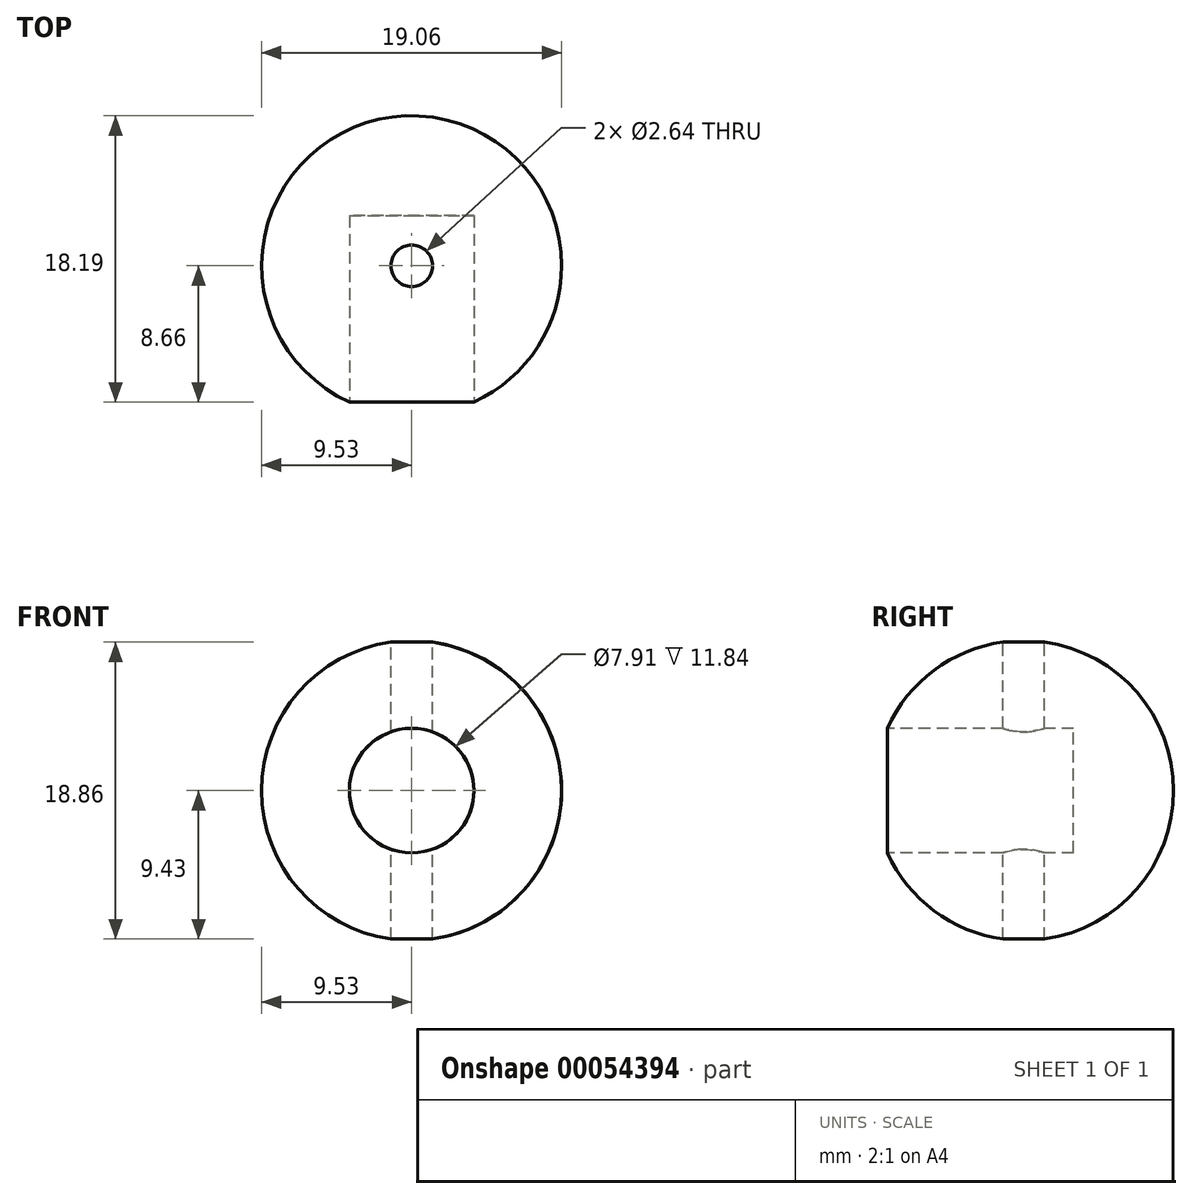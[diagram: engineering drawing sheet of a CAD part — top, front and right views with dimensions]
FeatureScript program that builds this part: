
annotation { "Feature Type Name" : "Feature", "Feature Type Description" : "" }
export const myFeature = defineFeature(function(context is Context, id is Id, definition is map)
    precondition{}
    {
        {
            var Q0;
            Q0=qCreatedBy(makeId("Front.planeOp"),FACE);
            var sketch = newSketch(context, id + "F0", { "sketchPlane" : qUnion([Q0])});
            skArc(sketch, "E0", {"start": v(0, -9.53) * mm, "mid": v(9.53, 0) * mm, "end": v(0, 9.53) * mm});
            skLineSegment(sketch, "E1", {"start": v(0, 9.53) * mm, "end": v(0, -9.53) * mm});
            skLineSegment(sketch, "E2", {"start": v(0, 0) * mm, "end": v(28.29, 0) * mm, "construction": true});
            skPoint(sketch, "E2.endSnap0", {"position": v(9.53, 0) * mm});
            skLineSegment(sketch, "E3", {"start": v(28.29, 0) * mm, "end": v(0, 0) * mm, "construction": true});
            skLineSegment(sketch, "E4", {"start": v(0, 0) * mm, "end": v(-27.51, 0) * mm, "construction": true});
            skSolve(sketch);
        }
        {
            var Q0;
            Q0=makeQuery(id+"F0.imprint","IMPRINT",FACE,{"disambiguationData":[TD([[makeQuery(id+"F0.imprint","IMPRINT",EDGE,{"derivedFrom":sQuery(id+"F0.wireOp",EDGE,"E0")}),1.0]])]});
            var Q1;
            Q1=sQuery(id+"F0.wireOp",EDGE,"E1");
            revolve(context, id + "F1", {"entities" : qUnion([Q0]), "axis" : qUnion([Q1]), "revolveType" : RevolveType.FULL});
        }
        {
            var Q0;
            Q0=qCreatedBy(makeId("Front.planeOp"),FACE);
            cPlane(context, id + "F2", {"entities" : qUnion([Q0]), "cplaneType" : CPlaneType.OFFSET, "offset" : 9.52 * mm, "width" : 152.4 * mm, "height" : 152.4 * mm});
        }
        {
            var Q0;
            Q0=qCreatedBy(id+"F2.planeOp",FACE);
            var sketch = newSketch(context, id + "F3", { "sketchPlane" : qUnion([Q0])});
            skCircle(sketch, "E5", {"center": v(0, 0) * mm, "radius": 3.96 * mm});
            skSolve(sketch);
        }
        {
            var Q0;
            Q0 = qSketchRegion(id + "F3", true);
            extrude(context, id + "F4", {"entities" : qUnion([Q0]), "operationType" : NewBodyOperationType.REMOVE, "oppositeDirection" : true, "depth" : 12.7 * mm});
        }
        {
            var Q0;
            Q0=qCreatedBy(makeId("Top.planeOp"),FACE);
            cPlane(context, id + "F5", {"entities" : qUnion([Q0]), "cplaneType" : CPlaneType.OFFSET, "offset" : 9.52 * mm, "width" : 152.4 * mm, "height" : 152.4 * mm});
        }
        {
            var Q0;
            Q0=qCreatedBy(id+"F5.planeOp",FACE);
            var sketch = newSketch(context, id + "F6", { "sketchPlane" : qUnion([Q0])});
            skCircle(sketch, "E6", {"center": v(0, 0) * mm, "radius": 1.32 * mm});
            skSolve(sketch);
        }
        {
            var Q0;
            Q0 = qSketchRegion(id + "F6", true);
            extrude(context, id + "F7", {"entities" : qUnion([Q0]), "operationType" : NewBodyOperationType.REMOVE, "endBound" : BoundingType.THROUGH_ALL, "oppositeDirection" : true, "depth" : 25.4 * mm});
        }
    });
